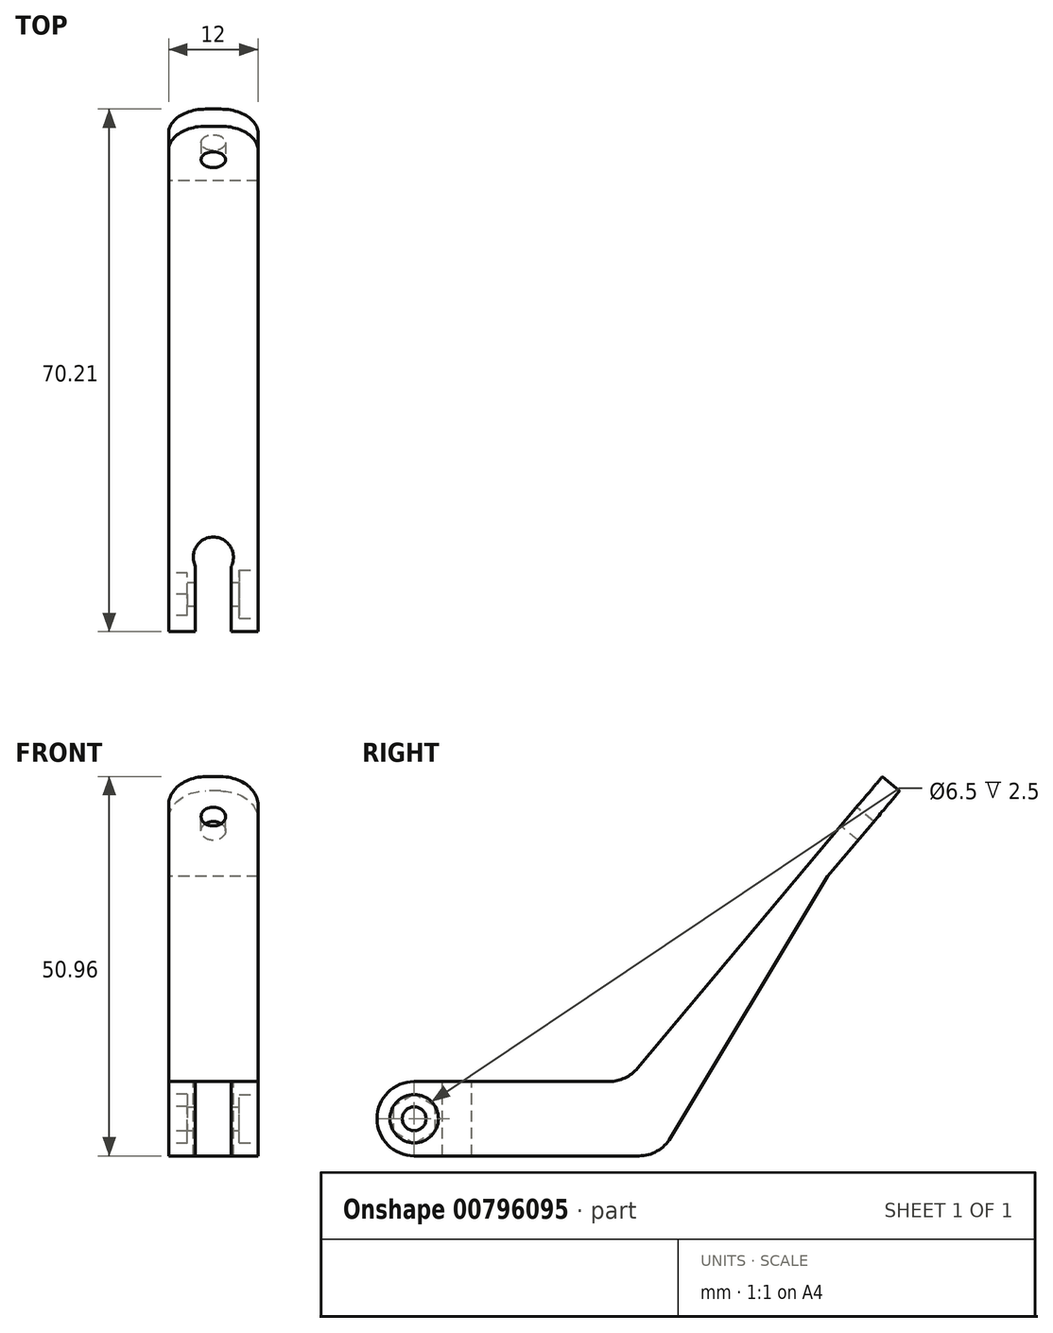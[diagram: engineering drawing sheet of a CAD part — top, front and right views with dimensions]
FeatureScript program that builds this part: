
annotation { "Feature Type Name" : "Feature", "Feature Type Description" : "" }
export const myFeature = defineFeature(function(context is Context, id is Id, definition is map)
    precondition{}
    {
        {
            var Q0;
            Q0=qCreatedBy(makeId("Right.planeOp"),FACE);
            var sketch = newSketch(context, id + "F0", { "sketchPlane" : qUnion([Q0])});
            skLineSegment(sketch, "E0.bottom", {"start": v(-19, -5) * mm, "end": v(19, -5) * mm});
            skLineSegment(sketch, "E0.top", {"start": v(-19, 5) * mm, "end": v(19, 5) * mm});
            skLineSegment(sketch, "E0.left", {"start": v(-19, -5) * mm, "end": v(-19, 5) * mm});
            skLineSegment(sketch, "E0.right", {"start": v(19, -5) * mm, "end": v(19, 5) * mm});
            skPoint(sketch, "E0.middle", {"position": v(0, 0) * mm});
            skLineSegment(sketch, "E1", {"start": v(19, -5) * mm, "end": v(10.34, 0) * mm});
            skLineSegment(sketch, "E2", {"start": v(10.34, 0) * mm, "end": v(48.9, 45.96) * mm});
            skLineSegment(sketch, "E3", {"start": v(48.9, 45.96) * mm, "end": v(51.2, 44.03) * mm});
            skLineSegment(sketch, "E4", {"start": v(41.56, 32.54) * mm, "end": v(19, -5) * mm});
            skLineSegment(sketch, "E5", {"start": v(51.2, 44.03) * mm, "end": v(41.56, 32.54) * mm});
            skSolve(sketch);
        }
        {
            var Q0;
            Q0 = qSketchRegion(id + "F0", true);
            extrude(context, id + "F1", {"entities" : qUnion([Q0]), "depth" : 12 * mm, "offsetDistance" : 25 * mm});
        }
        {
            var Q0;
            Q0=makeQuery(id+"F1.opExtrude","SWEPT_FACE",FACE,{"disambiguationData":[OSD([sQuery(id+"F0.wireOp",EDGE,"E0.top")])]});
            var sketch = newSketch(context, id + "F2", { "sketchPlane" : qUnion([Q0])});
            skCircle(sketch, "E6", {"center": v(6, -9) * mm, "radius": 2.7 * mm});
            skPoint(sketch, "E7", {"position": v(6, -19) * mm});
            skLineSegment(sketch, "E8.bottom", {"start": v(3.6, -19) * mm, "end": v(8.4, -19) * mm});
            skLineSegment(sketch, "E8.top", {"start": v(3.6, -10.24) * mm, "end": v(8.4, -10.24) * mm});
            skLineSegment(sketch, "E8.left", {"start": v(3.6, -19) * mm, "end": v(3.6, -10.24) * mm});
            skLineSegment(sketch, "E8.right", {"start": v(8.4, -19) * mm, "end": v(8.4, -10.24) * mm});
            skSolve(sketch);
        }
        {
            var Q0;
            Q0 = qSketchRegion(id + "F2", true);
            extrude(context, id + "F3", {"entities" : qUnion([Q0]), "operationType" : NewBodyOperationType.REMOVE, "oppositeDirection" : true, "depth" : 25 * mm, "offsetDistance" : 25 * mm});
        }
        {
            var Q0;
            Q0=makeQuery(id+"F1.opExtrude","CAP_FACE",FACE,{"disambiguationData":[OSD([sQuery(id+"F0.wireOp",EDGE,"E0.bottom"),sQuery(id+"F0.wireOp",EDGE,"E0.top"),sQuery(id+"F0.wireOp",EDGE,"E0.left"),sQuery(id+"F0.wireOp",EDGE,"E2"),sQuery(id+"F0.wireOp",EDGE,"E3"),sQuery(id+"F0.wireOp",EDGE,"E4")])],"isStart":false});
            var sketch = newSketch(context, id + "F4", { "sketchPlane" : qUnion([Q0])});
            skCircle(sketch, "E9", {"center": v(-14, 0) * mm, "radius": 1.6 * mm});
            skCircle(sketch, "E10", {"center": v(-14, 0) * mm, "radius": 3.25 * mm});
            skSolve(sketch);
        }
        {
            var Q0;
            Q0=makeQuery(id+"F4.imprint","IMPRINT",FACE,{"disambiguationData":[TD([[makeQuery(id+"F4.imprint","IMPRINT",EDGE,{"derivedFrom":sQuery(id+"F4.wireOp",EDGE,"E9")}),1.0]])]});
            extrude(context, id + "F5", {"entities" : qUnion([Q0]), "operationType" : NewBodyOperationType.REMOVE, "endBound" : BoundingType.THROUGH_ALL, "oppositeDirection" : true, "depth" : 25 * mm, "offsetDistance" : 25 * mm});
        }
        {
            var Q0;
            Q0=makeQuery(id+"F4.imprint","IMPRINT",FACE,{"disambiguationData":[TD([[makeQuery(id+"F4.imprint","IMPRINT",EDGE,{"derivedFrom":sQuery(id+"F4.wireOp",EDGE,"E9")}),-1.0]])]});
            extrude(context, id + "F6", {"entities" : qUnion([Q0]), "operationType" : NewBodyOperationType.REMOVE, "oppositeDirection" : true, "depth" : 2.5 * mm, "offsetDistance" : 25 * mm});
        }
        {
            var Q0;
            Q0=makeQuery(id+"F1.opExtrude","CAP_FACE",FACE,{"disambiguationData":[OSD([sQuery(id+"F0.wireOp",EDGE,"E0.bottom"),sQuery(id+"F0.wireOp",EDGE,"E0.top"),sQuery(id+"F0.wireOp",EDGE,"E0.left"),sQuery(id+"F0.wireOp",EDGE,"E2"),sQuery(id+"F0.wireOp",EDGE,"E3"),sQuery(id+"F0.wireOp",EDGE,"E4")])],"isStart":true});
            var sketch = newSketch(context, id + "F7", { "sketchPlane" : qUnion([Q0])});
            skCircle(sketch, "E11.cCircle", {"center": v(14, 0) * mm, "radius": 2.85 * mm, "construction": true});
            skLineSegment(sketch, "E11.0", {"start": v(11.15, -1.65) * mm, "end": v(11.15, 1.65) * mm});
            skLineSegment(sketch, "E11.1", {"start": v(11.15, 1.65) * mm, "end": v(14, 3.3) * mm});
            skLineSegment(sketch, "E11.2", {"start": v(14, 3.3) * mm, "end": v(16.85, 1.65) * mm});
            skLineSegment(sketch, "E11.3", {"start": v(16.85, 1.65) * mm, "end": v(16.85, -1.65) * mm});
            skLineSegment(sketch, "E11.4", {"start": v(16.85, -1.65) * mm, "end": v(14, -3.3) * mm});
            skLineSegment(sketch, "E11.5", {"start": v(14, -3.3) * mm, "end": v(11.15, -1.65) * mm});
            skPoint(sketch, "E11.0.midPoint", {"position": v(11.15, 0) * mm});
            skSolve(sketch);
        }
        {
            var Q0;
            Q0 = qSketchRegion(id + "F7", true);
            extrude(context, id + "F8", {"entities" : qUnion([Q0]), "operationType" : NewBodyOperationType.REMOVE, "oppositeDirection" : true, "depth" : 2.5 * mm, "offsetDistance" : 25 * mm});
        }
        {
            var Q0;
            Q0=makeQuery(id+"F1.opExtrude","SWEPT_FACE",FACE,{"disambiguationData":[OSD([sQuery(id+"F0.wireOp",EDGE,"E2")])]});
            var sketch = newSketch(context, id + "F9", { "sketchPlane" : qUnion([Q0])});
            skCircle(sketch, "E12", {"center": v(6, 59.65) * mm, "radius": 1.65 * mm});
            skPoint(sketch, "E13", {"position": v(6, 66.65) * mm});
            skSolve(sketch);
        }
        {
            var Q0;
            Q0 = qSketchRegion(id + "F9", true);
            extrude(context, id + "F10", {"entities" : qUnion([Q0]), "operationType" : NewBodyOperationType.REMOVE, "endBound" : BoundingType.THROUGH_ALL, "oppositeDirection" : true, "depth" : 25 * mm, "offsetDistance" : 25 * mm});
        }
        {
            var Q0;
            {var subQ0=sQuery(id+"F0.wireOp",EDGE,"E0.left");var subQ1=sQuery(id+"F0.wireOp",EDGE,"E0.top");Q0=makeQuery(id+"F3.boolean.opBoolean","SPLIT",EDGE,{"disambiguationData":[TD([makeQuery(id+"F3.opExtrude","SWEPT_FACE",FACE,{"disambiguationData":[OSD([sQuery(id+"F2.wireOp",EDGE,"E8.left")])]})])],"derivedFrom":makeQuery(id+"F1.opExtrude","SWEPT_EDGE",EDGE,{"disambiguationData":[OSD([subQ1,subQ0])]})});}
            var Q1;
            {var subQ0=sQuery(id+"F0.wireOp",EDGE,"E0.left");var subQ1=sQuery(id+"F0.wireOp",EDGE,"E0.top");Q1=makeQuery(id+"F3.boolean.opBoolean","SPLIT",EDGE,{"disambiguationData":[TD([makeQuery(id+"F3.opExtrude","SWEPT_FACE",FACE,{"disambiguationData":[OSD([sQuery(id+"F2.wireOp",EDGE,"E8.right")])]})])],"derivedFrom":makeQuery(id+"F1.opExtrude","SWEPT_EDGE",EDGE,{"disambiguationData":[OSD([subQ1,subQ0])]})});}
            var Q2;
            {var subQ0=sQuery(id+"F0.wireOp",EDGE,"E0.bottom");var subQ1=sQuery(id+"F0.wireOp",EDGE,"E0.left");Q2=makeQuery(id+"F3.boolean.opBoolean","SPLIT",EDGE,{"disambiguationData":[TD([makeQuery(id+"F3.opExtrude","SWEPT_FACE",FACE,{"disambiguationData":[OSD([sQuery(id+"F2.wireOp",EDGE,"E8.left")])]})])],"derivedFrom":makeQuery(id+"F1.opExtrude","SWEPT_EDGE",EDGE,{"disambiguationData":[OSD([subQ0,subQ1])]})});}
            var Q3;
            {var subQ0=sQuery(id+"F0.wireOp",EDGE,"E0.bottom");var subQ1=sQuery(id+"F0.wireOp",EDGE,"E0.left");Q3=makeQuery(id+"F3.boolean.opBoolean","SPLIT",EDGE,{"disambiguationData":[TD([makeQuery(id+"F3.opExtrude","SWEPT_FACE",FACE,{"disambiguationData":[OSD([sQuery(id+"F2.wireOp",EDGE,"E8.right")])]})])],"derivedFrom":makeQuery(id+"F1.opExtrude","SWEPT_EDGE",EDGE,{"disambiguationData":[OSD([subQ0,subQ1])]})});}
            var Q4;
            Q4=makeQuery(id+"F1.opExtrude","CAP_EDGE",EDGE,{"disambiguationData":[OSD([sQuery(id+"F0.wireOp",EDGE,"E3")])],"isStart":false});
            var Q5;
            Q5=makeQuery(id+"F1.opExtrude","CAP_EDGE",EDGE,{"disambiguationData":[OSD([sQuery(id+"F0.wireOp",EDGE,"E3")])],"isStart":true});
            var Q6;
            Q6=makeQuery(id+"F1.opExtrude","SWEPT_EDGE",EDGE,{"disambiguationData":[OSD([sQuery(id+"F0.wireOp",EDGE,"E0.top"),sQuery(id+"F0.wireOp",EDGE,"E2")])]});
            var Q7;
            Q7=makeQuery(id+"F1.opExtrude","SWEPT_EDGE",EDGE,{"disambiguationData":[OSD([sQuery(id+"F0.wireOp",EDGE,"E0.bottom"),sQuery(id+"F0.wireOp",EDGE,"E0.right"),sQuery(id+"F0.wireOp",EDGE,"E1"),sQuery(id+"F0.wireOp",EDGE,"E4")])]});
            fillet(context, id + "F11", {"entities" : qUnion([Q0, Q1, Q2, Q3, Q4, Q5, Q6, Q7]), "radius" : 5 * mm, "tangentPropagation" : true, "allowEdgeOverflow" : false});
        }
    });
